# Revit family: PRD_FrankeWS_SlbUrnls_ConnectionPlateForTroughUrinal_ZCMPX0008
name_source: partatom
category: Plumbing Fixtures
revit_build: Autodesk Revit 2018 (Build: 20190510_1515(x64)
units: mm (PartAtom-declared; Revit-internal decimal feet)

## family parameters
Always vertical = No
Cut with Voids When Loaded = No
OmniClass Number = 23.40.20.21
OmniClass Title = Toilet and Bath Specialties
Part Type = Normal
Room Calculation Point = No
Round Connector Dimension = Use Diameter
Shared = Yes
Work Plane-Based = No

## types (1)
- ZCMPX0008
    AssetType = Fixed
    BIMObjectName = PRD_AR_SlabUrinals_ConnectionPlateForTroughUrinal_ZCMPX0008
    Category = Pr_40_20_93_77, Slab urinals
    Color = Stainless steel
    ConnectionPlateMaterial = PRD_AR_StainlessSteel_SatinFinished
    Description = Connection plate for trough urinal NIAGARA CMPX551 - CMPX555, stainless steel, surface satin finished, material thickness 1 mm. To cover the related joint of urinal combinations.
    DurationUnit = year
    Features = Connection plate trough urinal
    Finish = Satin finished
    IfcExportAs = IfcBuildingElementProxy
    IfcExportType = NOTDEFINED
    Manufacturer = KWC Group AG
    ManufacturerName = KWC Group AG
    ManufacturerURL = www.kwc.com
    Material = Stainless steel
    Model = ZCMPX0008
    ModelNumber = 2000101123
    ModelReference = ZCMPX0008
    NBSDescription = Urinal assembly
    NBSReference = 45-35-70/352
    Name = Connection plate for trough urinal ZCMPX0008
    NominalHeight = 365 mm
    NominalLength = 38 mm
    NominalWidth = 9 mm  [stored 0.0295276 ft]
    ProductInformation = https://pim.kwc.com
    URL = www.kwc.com
    Uniclass2015Code = Pr_40_20_93_77
    Uniclass2015Title = Slab urinals
    Uniclass2015Version = Products v1.5
    Version = 1
    WarrantyDurationUnit = year

note: [stored X ft] marks values corroborated as IEEE doubles in the binary element streams (Revit-internal decimal feet)

## geometry (parser evidence)
native form markers: Sweep x2
no freeform markers — native parametric forms only
